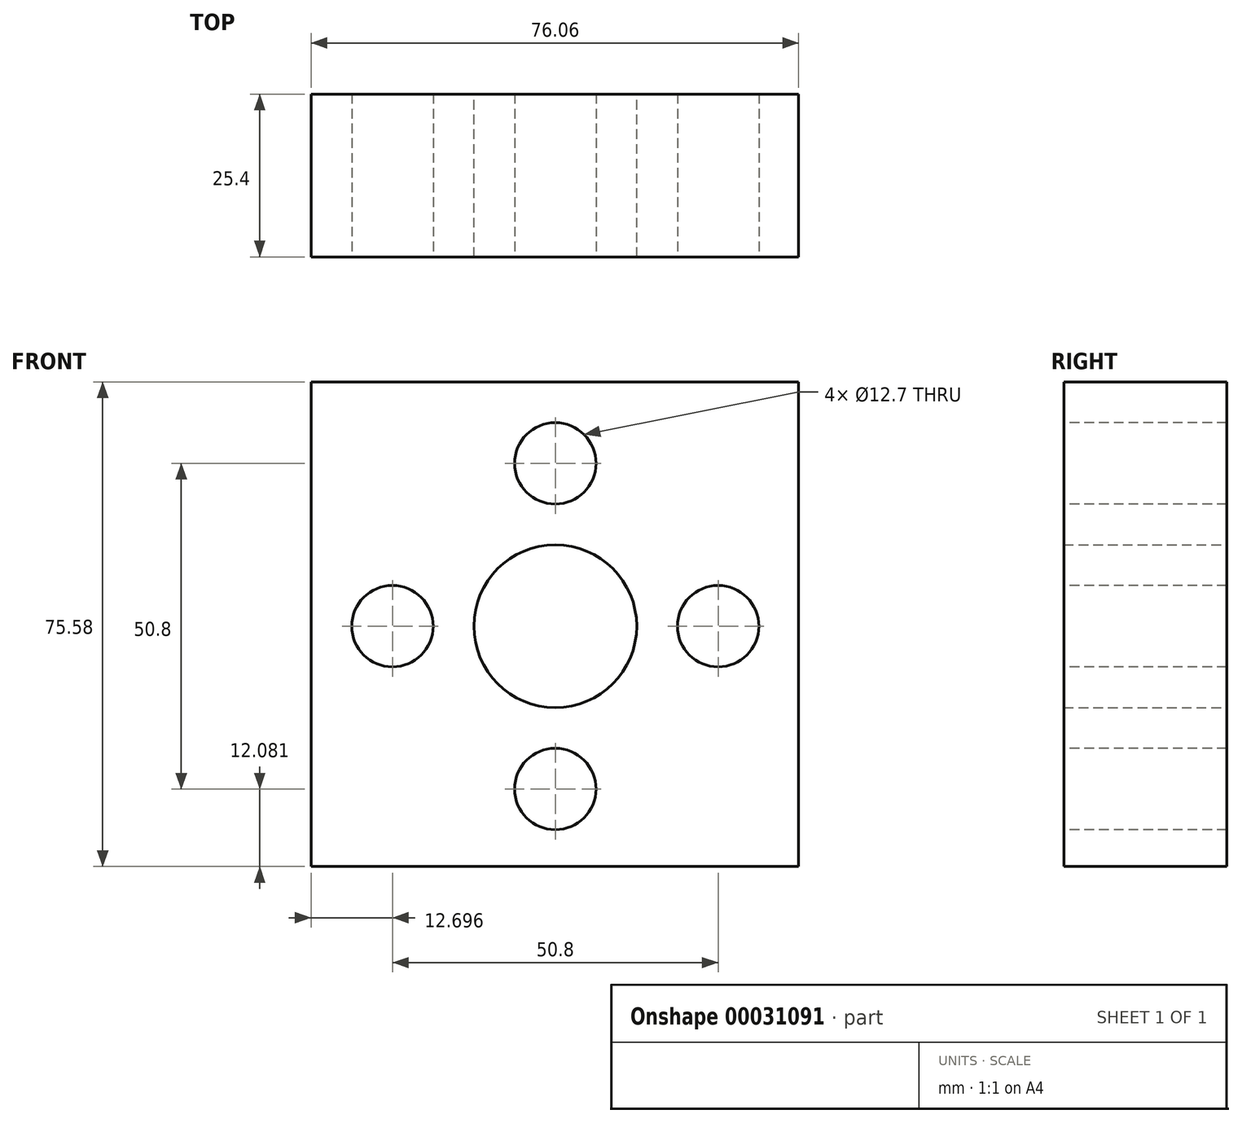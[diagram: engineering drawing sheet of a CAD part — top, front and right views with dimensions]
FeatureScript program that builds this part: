
annotation { "Feature Type Name" : "Feature", "Feature Type Description" : "" }
export const myFeature = defineFeature(function(context is Context, id is Id, definition is map)
    precondition{}
    {
        {
            var Q0;
            Q0=qCreatedBy(makeId("Front.planeOp"),FACE);
            var sketch = newSketch(context, id + "F0", { "sketchPlane" : qUnion([Q0])});
            skLineSegment(sketch, "E0.bottom", {"start": v(0, 0) * mm, "end": v(-76.06, 0) * mm});
            skLineSegment(sketch, "E0.top", {"start": v(0, 75.58) * mm, "end": v(-76.06, 75.58) * mm});
            skLineSegment(sketch, "E0.left", {"start": v(0, 0) * mm, "end": v(0, 75.58) * mm});
            skLineSegment(sketch, "E0.right", {"start": v(-76.06, 0) * mm, "end": v(-76.06, 75.58) * mm});
            skSolve(sketch);
        }
        {
            var Q0;
            Q0=makeQuery(id+"F0.imprint","IMPRINT",FACE,{"disambiguationData":[TD([[makeQuery(id+"F0.imprint","IMPRINT",EDGE,{"derivedFrom":sQuery(id+"F0.wireOp",EDGE,"E0.bottom")}),-1.0]])]});
            extrude(context, id + "F1", {"entities" : qUnion([Q0]), "depth" : 25.4 * mm});
        }
        {
            var Q0;
            Q0=makeQuery(id+"F1.opExtrude","CAP_FACE",FACE,{"disambiguationData":[OSD([sQuery(id+"F0.wireOp",EDGE,"E0.bottom"),sQuery(id+"F0.wireOp",EDGE,"E0.top"),sQuery(id+"F0.wireOp",EDGE,"E0.left"),sQuery(id+"F0.wireOp",EDGE,"E0.right")])],"isStart":true});
            var sketch = newSketch(context, id + "F2", { "sketchPlane" : qUnion([Q0])});
            skCircle(sketch, "E1", {"center": v(37.96, 37.48) * mm, "radius": 12.7 * mm});
            skSolve(sketch);
        }
        {
            var Q0;
            Q0 = qSketchRegion(id + "F2", true);
            extrude(context, id + "F3", {"entities" : qUnion([Q0]), "operationType" : NewBodyOperationType.REMOVE, "endBound" : BoundingType.THROUGH_ALL, "oppositeDirection" : true, "depth" : 25.4 * mm});
        }
        {
            var Q0;
            Q0=makeQuery(id+"F1.opExtrude","CAP_FACE",FACE,{"disambiguationData":[OSD([sQuery(id+"F0.wireOp",EDGE,"E0.bottom"),sQuery(id+"F0.wireOp",EDGE,"E0.top"),sQuery(id+"F0.wireOp",EDGE,"E0.left"),sQuery(id+"F0.wireOp",EDGE,"E0.right")])],"isStart":false});
            var sketch = newSketch(context, id + "F4", { "sketchPlane" : qUnion([Q0])});
            skCircle(sketch, "E2", {"center": v(-37.96, 62.88) * mm, "radius": 6.35 * mm});
            skCircle(sketch, "E3", {"center": v(-63.36, 37.48) * mm, "radius": 6.35 * mm});
            skCircle(sketch, "E4", {"center": v(-37.96, 37.48) * mm, "radius": 25.4 * mm, "construction": true});
            skLineSegment(sketch, "E5", {"start": v(-37.96, 37.48) * mm, "end": v(-37.96, 62.88) * mm, "construction": true});
            skLineSegment(sketch, "E6", {"start": v(-37.96, 37.48) * mm, "end": v(-63.36, 37.48) * mm, "construction": true});
            skLineSegment(sketch, "E7", {"start": v(-37.96, 37.48) * mm, "end": v(-12.56, 37.48) * mm, "construction": true});
            skLineSegment(sketch, "E8", {"start": v(-37.96, 37.48) * mm, "end": v(-37.96, 12.08) * mm, "construction": true});
            skCircle(sketch, "E9", {"center": v(-37.96, 12.08) * mm, "radius": 6.35 * mm});
            skCircle(sketch, "E10", {"center": v(-12.56, 37.48) * mm, "radius": 6.35 * mm});
            skSolve(sketch);
        }
        {
            var Q0;
            Q0 = qSketchRegion(id + "F4", true);
            extrude(context, id + "F5", {"entities" : qUnion([Q0]), "operationType" : NewBodyOperationType.REMOVE, "endBound" : BoundingType.THROUGH_ALL, "oppositeDirection" : true, "depth" : 25.4 * mm});
        }
    });
